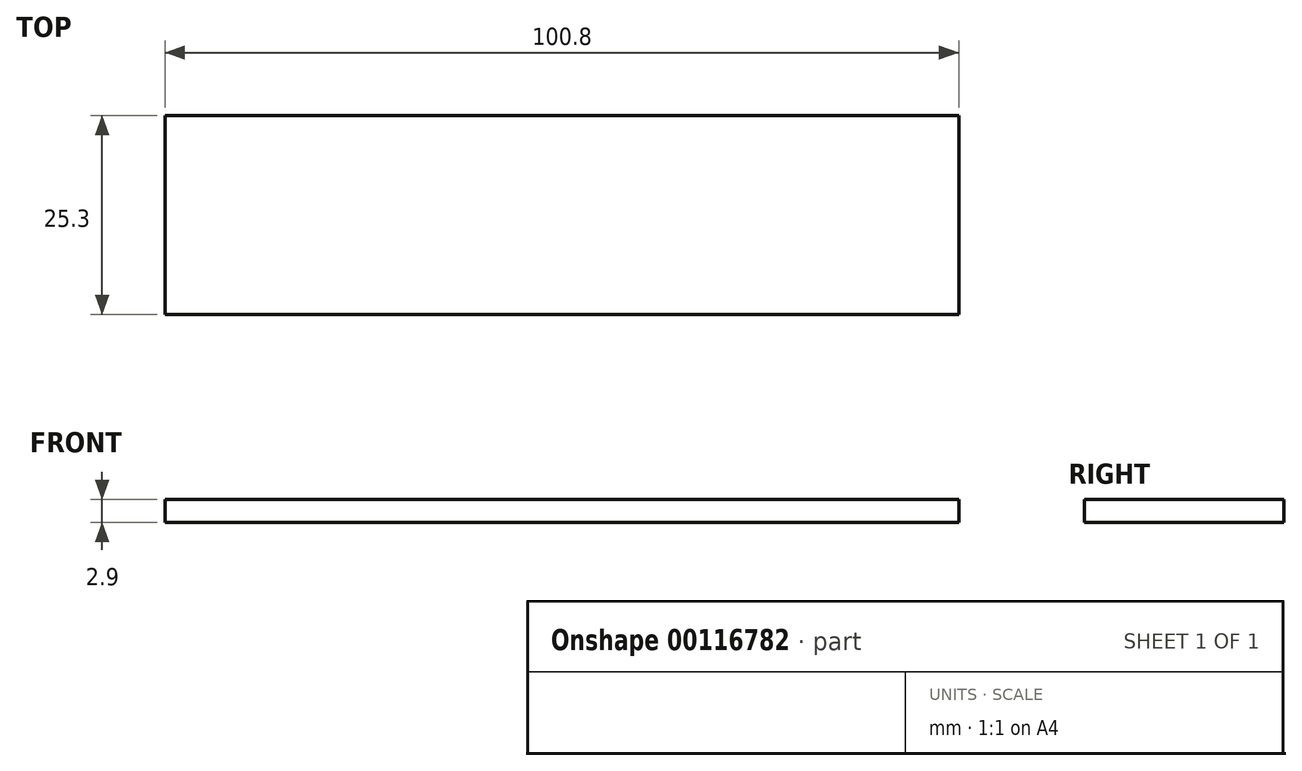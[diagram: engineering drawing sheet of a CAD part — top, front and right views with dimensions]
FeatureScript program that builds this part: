
annotation { "Feature Type Name" : "Feature", "Feature Type Description" : "" }
export const myFeature = defineFeature(function(context is Context, id is Id, definition is map)
    precondition{}
    {
        {
            var Q0;
            Q0=qCreatedBy(makeId("Top.planeOp"),FACE);
            var sketch = newSketch(context, id + "F0", { "sketchPlane" : qUnion([Q0])});
            skLineSegment(sketch, "E0.bottom", {"start": v(50.4, -12.65) * mm, "end": v(-50.4, -12.65) * mm});
            skLineSegment(sketch, "E0.top", {"start": v(50.4, 12.65) * mm, "end": v(-50.4, 12.65) * mm});
            skLineSegment(sketch, "E0.left", {"start": v(50.4, -12.65) * mm, "end": v(50.4, 12.65) * mm});
            skLineSegment(sketch, "E0.right", {"start": v(-50.4, -12.65) * mm, "end": v(-50.4, 12.65) * mm});
            skPoint(sketch, "E0.middle", {"position": v(0, 0) * mm});
            skSolve(sketch);
        }
        {
            var Q0;
            Q0=makeQuery(id+"F0.imprint","IMPRINT",FACE,{"disambiguationData":[TD([[makeQuery(id+"F0.imprint","IMPRINT",EDGE,{"derivedFrom":sQuery(id+"F0.wireOp",EDGE,"E0.bottom")}),-1.0]])]});
            extrude(context, id + "F1", {"entities" : qUnion([Q0]), "depth" : 2.9 * mm});
        }
    });
